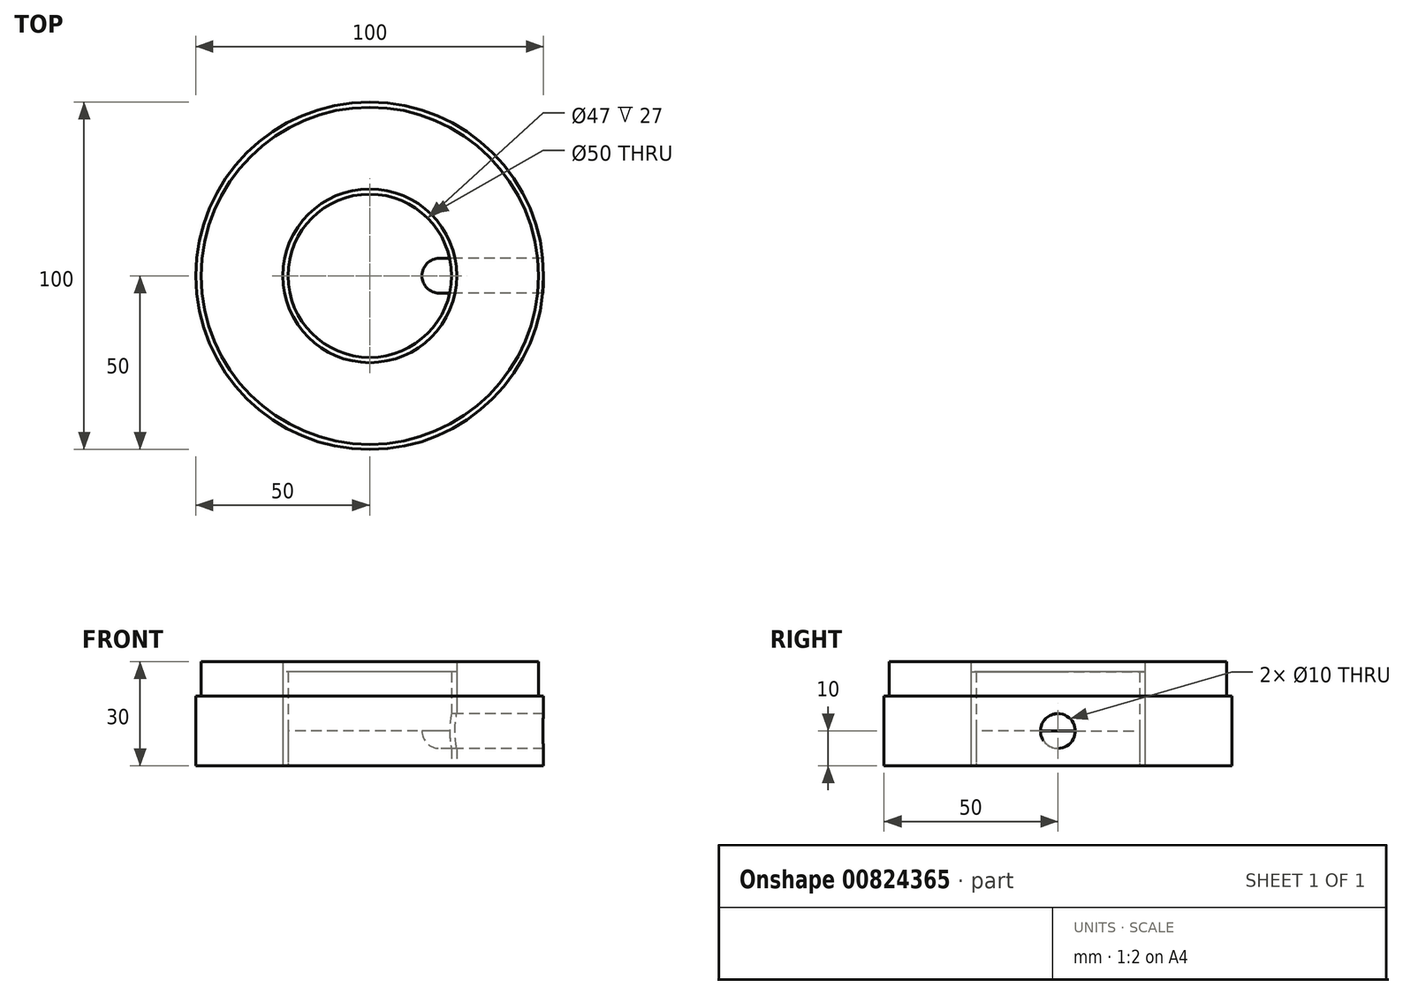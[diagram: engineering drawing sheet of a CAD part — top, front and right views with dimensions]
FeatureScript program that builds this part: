
annotation { "Feature Type Name" : "Feature", "Feature Type Description" : "" }
export const myFeature = defineFeature(function(context is Context, id is Id, definition is map)
    precondition{}
    {
        {
            var Q0;
            Q0=qCreatedBy(makeId("Top.planeOp"),FACE);
            var sketch = newSketch(context, id + "F0", { "sketchPlane" : qUnion([Q0])});
            skCircle(sketch, "E0", {"center": v(0, 0) * mm, "radius": 50 * mm});
            skCircle(sketch, "E1", {"center": v(0, 0) * mm, "radius": 48.5 * mm});
            skCircle(sketch, "E2", {"center": v(0, 0) * mm, "radius": 25 * mm});
            skCircle(sketch, "E3", {"center": v(0, 0) * mm, "radius": 23.5 * mm});
            skSolve(sketch);
        }
        {
            var Q0;
            Q0=makeQuery(id+"F0.imprint","IMPRINT",FACE,{"disambiguationData":[TD([[makeQuery(id+"F0.imprint","IMPRINT",EDGE,{"derivedFrom":sQuery(id+"F0.wireOp",EDGE,"E3")}),1.0]])]});
            extrude(context, id + "F1", {"entities" : qUnion([Q0]), "depth" : 10 * mm, "offsetDistance" : 25 * mm});
        }
        {
            var Q0;
            Q0=makeQuery(id+"F0.imprint","IMPRINT",FACE,{"disambiguationData":[TD([[makeQuery(id+"F0.imprint","IMPRINT",EDGE,{"derivedFrom":sQuery(id+"F0.wireOp",EDGE,"E2")}),1.0]])]});
            var Q1;
            Q1=sQuery(id+"F0.wireOp",EDGE,"E2");
            extrude(context, id + "F2", {"entities" : qUnion([Q0]), "surfaceEntities" : qUnion([Q1]), "depth" : 27 * mm, "offsetDistance" : 25 * mm});
        }
        {
            var Q0;
            Q0=makeQuery(id+"F0.imprint","IMPRINT",FACE,{"disambiguationData":[TD([[makeQuery(id+"F0.imprint","IMPRINT",EDGE,{"derivedFrom":sQuery(id+"F0.wireOp",EDGE,"E1")}),1.0]])]});
            extrude(context, id + "F3", {"entities" : qUnion([Q0]), "depth" : 30 * mm, "offsetDistance" : 25 * mm});
        }
        {
            var Q0;
            Q0 = qSketchRegion(id + "F0", true);
            extrude(context, id + "F4", {"entities" : qUnion([Q0]), "operationType" : NewBodyOperationType.ADD, "depth" : 20 * mm, "offsetDistance" : 25 * mm});
        }
        {
            var Q0;
            Q0=qCreatedBy(makeId("Right.planeOp"),FACE);
            cPlane(context, id + "F5", {"entities" : qUnion([Q0]), "cplaneType" : CPlaneType.OFFSET, "offset" : 20 * mm, "width" : 150 * mm, "height" : 150 * mm});
        }
        {
            var Q0;
            Q0=qCreatedBy(id+"F5.planeOp",FACE);
            var sketch = newSketch(context, id + "F6", { "sketchPlane" : qUnion([Q0])});
            skCircle(sketch, "E4", {"center": v(0, 10) * mm, "radius": 5 * mm});
            skSolve(sketch);
        }
        {
            var Q0;
            Q0=makeQuery(id+"F6.imprint","IMPRINT",FACE,{"disambiguationData":[TD([[makeQuery(id+"F6.imprint","IMPRINT",EDGE,{"derivedFrom":sQuery(id+"F6.wireOp",EDGE,"E4")}),1.0]])]});
            extrude(context, id + "F7", {"entities" : qUnion([Q0]), "operationType" : NewBodyOperationType.REMOVE, "depth" : 90 * mm, "offsetDistance" : 25 * mm});
        }
        {
            var Q0;
            Q0=qCreatedBy(makeId("Top.planeOp"),FACE);
            cPlane(context, id + "F8", {"entities" : qUnion([Q0]), "cplaneType" : CPlaneType.OFFSET, "offset" : 10 * mm, "width" : 150 * mm, "height" : 150 * mm});
        }
        {
            var Q0;
            Q0=qCreatedBy(id+"F8.planeOp",FACE);
            var sketch = newSketch(context, id + "F9", { "sketchPlane" : qUnion([Q0])});
            skLineSegment(sketch, "E5", {"start": v(20, 0) * mm, "end": v(20, 5) * mm});
            skArc(sketch, "E6", {"start": v(20, 5) * mm, "mid": v(15, 0) * mm, "end": v(20, -5) * mm});
            skLineSegment(sketch, "E7", {"start": v(20, 0) * mm, "end": v(20, -5) * mm});
            skSolve(sketch);
        }
        {
            var Q0;
            Q0=makeQuery(id+"F9.imprint","IMPRINT",FACE,{"disambiguationData":[TD([[makeQuery(id+"F9.imprint","IMPRINT",EDGE,{"derivedFrom":sQuery(id+"F9.wireOp",EDGE,"1AUyJRVU-xp1U-BeT1-CYQk-XZoLwzfYLCDu")}),1.0]])]});
            var Q1;
            Q1=makeQuery(id+"F9.imprint","IMPRINT",FACE,{"disambiguationData":[TD([[makeQuery(id+"F9.imprint","IMPRINT",EDGE,{"derivedFrom":sQuery(id+"F9.wireOp",EDGE,"E5")}),1.0]])]});
            var Q2;
            Q2=sQuery(id+"F9.wireOp",EDGE,"1AUyJRVU-xp1U-BeT1-CYQk-XZoLwzfYLCDu");
            var Q3;
            Q3=makeQuery(id+"F7.boolean.opBoolean","INTERSECT",EDGE,{"derivedFrom":[makeQuery(id+"F1.opExtrude","CAP_FACE",FACE,{"disambiguationData":[OSD([sQuery(id+"F0.wireOp",EDGE,"E3")])],"isStart":false}),makeQuery(id+"F7.opExtrude","CAP_FACE",FACE,{"disambiguationData":[OSD([sQuery(id+"F6.wireOp",EDGE,"E4")])],"isStart":true})]});
            revolve(context, id + "F10", {"operationType" : NewBodyOperationType.REMOVE, "surfaceOperationType" : NewSurfaceOperationType.NEW, "entities" : qUnion([Q0, Q1]), "surfaceEntities" : qUnion([Q2]), "axis" : qUnion([Q3]), "revolveType" : RevolveType.ONE_DIRECTION, "oppositeDirection" : true, "angle" : 91 * degree});
        }
    });
